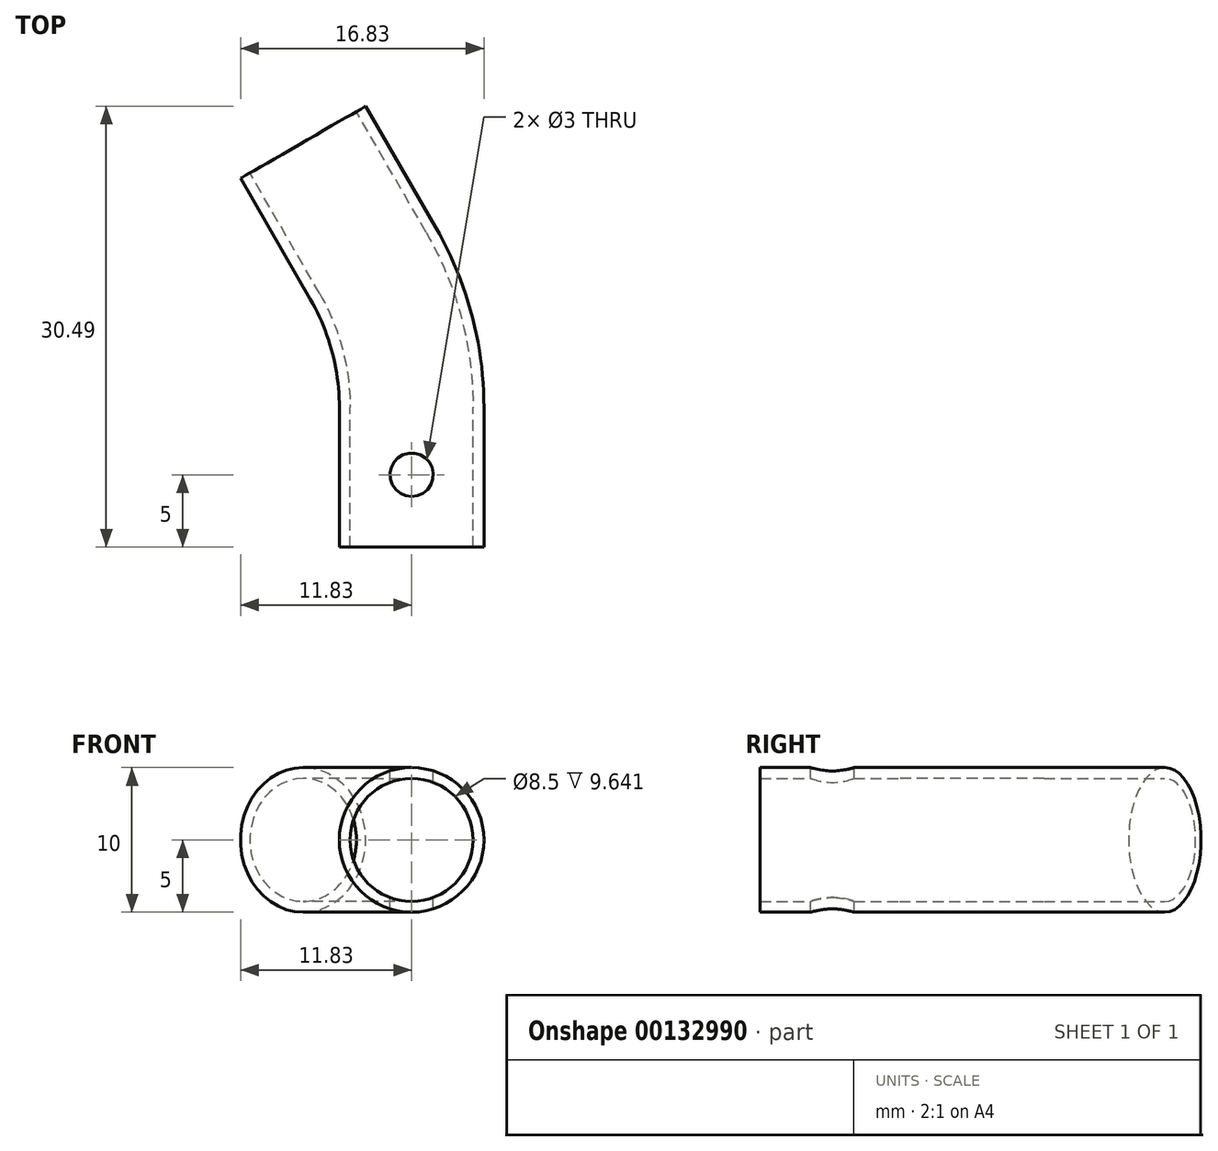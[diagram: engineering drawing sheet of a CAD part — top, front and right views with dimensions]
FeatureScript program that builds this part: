
annotation { "Feature Type Name" : "Feature", "Feature Type Description" : "" }
export const myFeature = defineFeature(function(context is Context, id is Id, definition is map)
    precondition{}
    {
        {
            var Q0;
            Q0=qCreatedBy(makeId("Top.planeOp"),FACE);
            var sketch = newSketch(context, id + "F0", { "sketchPlane" : qUnion([Q0])});
            skLineSegment(sketch, "E0", {"start": v(0, 0) * mm, "end": v(0, 9.64) * mm});
            skLineSegment(sketch, "E1", {"start": v(-2.68, 19.64) * mm, "end": v(-7.5, 28) * mm});
            skPoint(sketch, "E2.visualSharp", {"position": v(0, 15) * mm});
            skArc(sketch, "E2.filletArc", {"start": v(0, 9.64) * mm, "mid": v(-0.68, 14.82) * mm, "end": v(-2.68, 19.64) * mm});
            skSolve(sketch);
        }
        {
            var Q0;
            Q0=qCreatedBy(makeId("Front.planeOp"),FACE);
            var sketch = newSketch(context, id + "F1", { "sketchPlane" : qUnion([Q0])});
            skCircle(sketch, "E3", {"center": v(0, 0) * mm, "radius": 5 * mm});
            skCircle(sketch, "E4", {"center": v(0, 0) * mm, "radius": 4.25 * mm});
            skSolve(sketch);
        }
        {
            var Q0;
            Q0=makeQuery(id+"F1.imprint","IMPRINT",FACE,{"disambiguationData":[TD([[makeQuery(id+"F1.imprint","IMPRINT",EDGE,{"derivedFrom":sQuery(id+"F1.wireOp",EDGE,"E3")}),1.0]])]});
            var Q1;
            Q1=sQuery(id+"F0.wireOp",EDGE,"E0");
            var Q2;
            Q2=sQuery(id+"F0.wireOp",EDGE,"E2.filletArc");
            var Q3;
            Q3=sQuery(id+"F0.wireOp",EDGE,"E1");
            sweep(context, id + "F2", {"profiles" : qUnion([Q0]), "path" : qUnion([Q1, Q2, Q3])});
        }
        {
            var Q0;
            Q0=qCreatedBy(makeId("Top.planeOp"),FACE);
            var sketch = newSketch(context, id + "F3", { "sketchPlane" : qUnion([Q0])});
            skCircle(sketch, "E5", {"center": v(0, 5) * mm, "radius": 1.5 * mm});
            skSolve(sketch);
        }
        {
            var Q0;
            Q0 = qSketchRegion(id + "F3", true);
            extrude(context, id + "F4", {"entities" : qUnion([Q0]), "operationType" : NewBodyOperationType.REMOVE, "oppositeDirection" : true, "depth" : 25 * mm, "hasSecondDirection" : true, "secondDirectionOppositeDirection" : false, "secondDirectionDepth" : 25 * mm});
        }
    });
